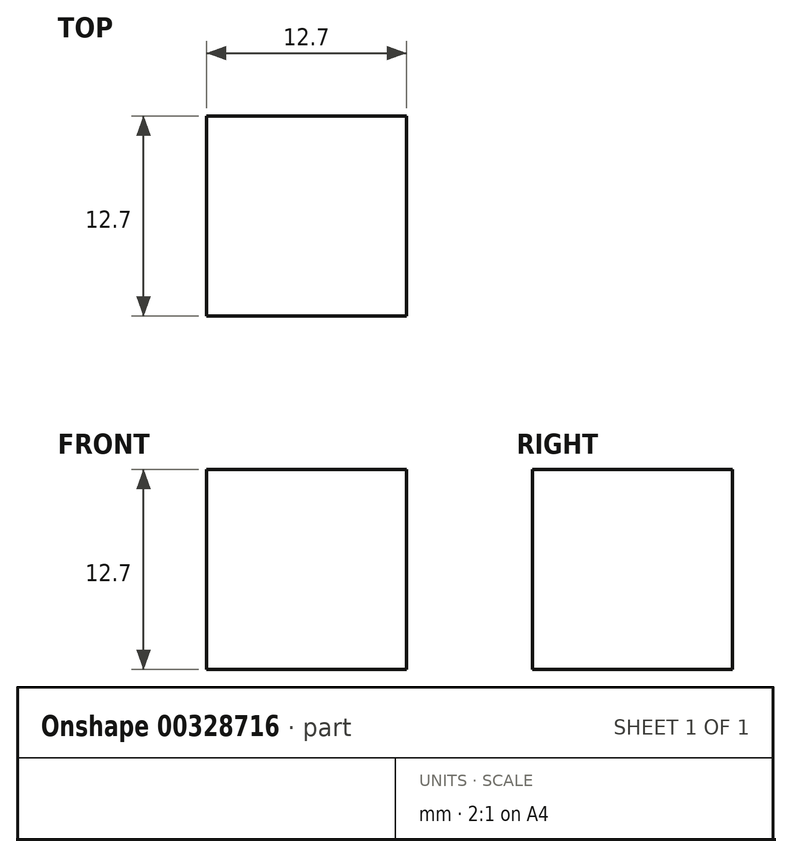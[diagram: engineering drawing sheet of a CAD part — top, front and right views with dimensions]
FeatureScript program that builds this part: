
annotation { "Feature Type Name" : "Feature", "Feature Type Description" : "" }
export const myFeature = defineFeature(function(context is Context, id is Id, definition is map)
    precondition{}
    {
        {
            var Q0;
            Q0=qCreatedBy(makeId("Top.planeOp"),FACE);
            var sketch = newSketch(context, id + "F0", { "sketchPlane" : qUnion([Q0])});
            skLineSegment(sketch, "E0.bottom", {"start": v(0, 0) * mm, "end": v(12.7, 0) * mm});
            skLineSegment(sketch, "E0.top", {"start": v(0, -12.7) * mm, "end": v(12.7, -12.7) * mm});
            skLineSegment(sketch, "E0.left", {"start": v(0, 0) * mm, "end": v(0, -12.7) * mm});
            skLineSegment(sketch, "E0.right", {"start": v(12.7, 0) * mm, "end": v(12.7, -12.7) * mm});
            skSolve(sketch);
        }
        {
            var Q0;
            Q0=makeQuery(id+"F0.imprint","IMPRINT",FACE,{"disambiguationData":[TD([[makeQuery(id+"F0.imprint","IMPRINT",EDGE,{"derivedFrom":sQuery(id+"F0.wireOp",EDGE,"E0.bottom")}),-1.0]])]});
            extrude(context, id + "F1", {"entities" : qUnion([Q0]), "depth" : 12.7 * mm});
        }
    });
